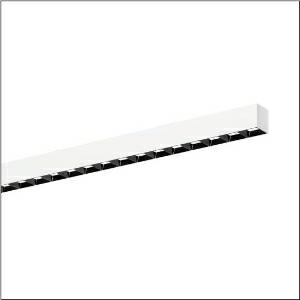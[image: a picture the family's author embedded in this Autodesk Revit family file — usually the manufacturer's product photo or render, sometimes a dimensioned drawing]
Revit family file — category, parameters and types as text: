
# Revit family: silica_21_51mx21da44wb
name_source: partatom
category: Lighting Fixtures
units: mm (PartAtom-declared; Revit-internal decimal feet)

## family parameters
Cut with Voids When Loaded = No
Host = Face
Light Source = No
Part Type = Normal
Room Calculation Point = No
Round Connector Dimension = Use Diameter
Shared = No

## types (1)
- --- (1 x LED, 4320 lm, 25.6 W, 4000K)
    Apparent Load = 26 VA
    CIE Flux Codes = 87 99 100 100 100
    Color Rendering = 80
    Color Temperature = 4000K
    Default Elevation = 1800 mm
    Description = Silica 21, office luminaire, primary light control with darklight reflector, of PMMA, black, CAT 2 (L<= 3000cd/m²), light emission: direct distribution, primary light characteristic: symmetric, installation type: surface-mounted, LED, rated luminous flux: 4.320lm, luminous efficacy: 169lm/W, light colour: 840, colour temperature: 4000K, control gear: DALI 2, with terminal, 3+2-pole, max. 2.5mm², mains connection: 220..240V, AC, 50/60Hz, rated input power: 25.6W, luminaire housing, of aluminium, traffic white (RAL 9016), length: 1.204mm, width: 53mm, height: 53mm, protection rating (complete): IP20, insulation class (complete): insulation class I (protective earthing), certification: CE, permissible operating ambient temperature: 0..+35°C, standard: EN 50419, packaging unit: 1 piece
    Height = 53 mm
    Lamp = 1 x LED
    Lamp Light Flux = 4320 lm
    Lamp Power = 25.6 W
    Lamp count = 1
    Length = 1204 mm
    Luminous efficacy = 169 lm/W
    Manufacturer = Siteco
    ModVariant = No
    Model = 51MX21DA44WB
    Mounting Place = Ceiling
    Mounting Type = Surface mounted
    Number of Poles = 1
    OnlyDefault = Yes
    Power Factor = 1
    Product Name = Silica 21
    Product group = office luminaire | ceiling mounted
    ProductGroupID = 301
    Protection Class = Protection class I
    Protection Degree = IP 20
    RLX_Detail_Level = 1
    RLX_Emergency_Light_Flux = 0 lm
    RLX_Emergency_Type = 0
    RLX_Emergency_Type_DB = No
    RlxData = <blob elided: 41069 chars, md5=646426a6>
    Socket = socket
    Standby Power = 0 W
    System Light Flux = 4320 lm
    System Power = 26 W
    Type Comments = factory setting: luminous flux: 100 % | dim-lin: 254 | 367 mA
    Type Image = l_1335873.jpg
    URL = http://relux.com
    VarID = @adj_028623
    Voltage = 0 V
    Weight = 0.00 kg
    Width = 53 mm

## geometry (parser evidence)
native form markers: Blend x4, Sweep x8
no freeform markers — native parametric forms only
